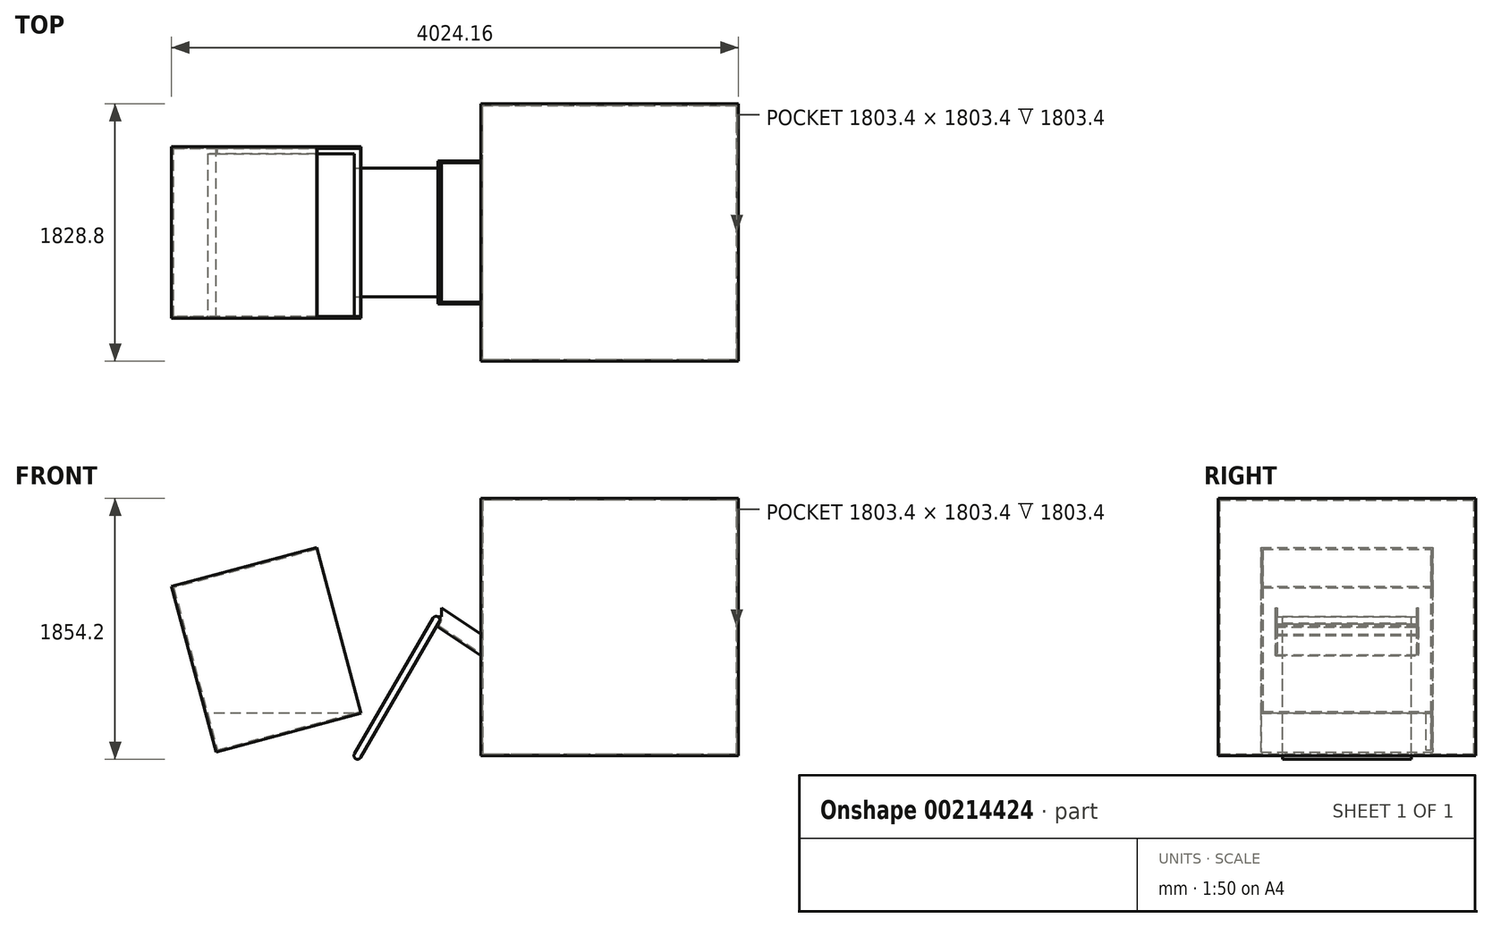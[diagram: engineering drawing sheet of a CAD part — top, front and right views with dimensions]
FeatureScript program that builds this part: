
annotation { "Feature Type Name" : "Feature", "Feature Type Description" : "" }
export const myFeature = defineFeature(function(context is Context, id is Id, definition is map)
    precondition{}
    {
        {
            var Q0;
            Q0=qCreatedBy(makeId("Front.planeOp"),FACE);
            var sketch = newSketch(context, id + "F0", { "sketchPlane" : qUnion([Q0])});
            skLineSegment(sketch, "E0", {"start": v(-22, 12.7) * mm, "end": v(535.26, 977.9) * mm});
            skCircle(sketch, "E1", {"center": v(557.26, 965.2) * mm, "radius": 25.4 * mm});
            skCircle(sketch, "E2", {"center": v(0, 0) * mm, "radius": 25.4 * mm});
            skLineSegment(sketch, "E3", {"start": v(22, -12.7) * mm, "end": v(579.26, 952.5) * mm});
            skLineSegment(sketch, "E4", {"start": v(569.96, 914.4) * mm, "end": v(874.76, 711.2) * mm});
            skLineSegment(sketch, "E5", {"start": v(874.76, 711.2) * mm, "end": v(874.76, 0) * mm});
            skLineSegment(sketch, "E6", {"start": v(874.76, 0) * mm, "end": v(2703.56, 0) * mm});
            skLineSegment(sketch, "E7", {"start": v(2703.56, 0) * mm, "end": v(2703.56, 1828.8) * mm});
            skLineSegment(sketch, "E8", {"start": v(2703.56, 1828.8) * mm, "end": v(874.76, 1828.8) * mm});
            skLineSegment(sketch, "E9", {"start": v(874.76, 1828.8) * mm, "end": v(874.76, 863.6) * mm});
            skLineSegment(sketch, "E10", {"start": v(874.76, 863.6) * mm, "end": v(569.96, 1066.8) * mm});
            skLineSegment(sketch, "E11", {"start": v(569.96, 1066.8) * mm, "end": v(569.96, 914.4) * mm});
            skSolve(sketch);
        }
        {
            var Q0;
            {var subQ7=sQuery(id+"F0.wireOp",EDGE,"E4");Q0=makeQuery(id+"F0.imprint","IMPRINT",FACE,{"disambiguationData":[TD([[makeQuery(id+"F0.imprint","IMPRINT",EDGE,{"derivedFrom":subQ7}),1.0]])]});}
            extrude(context, id + "F1", {"entities" : qUnion([Q0]), "endBound" : BoundingType.SYMMETRIC, "depth" : 1828.8 * mm});
        }
        {
            var Q0;
            {var subQ7=sQuery(id+"F0.wireOp",EDGE,"E0");Q0=makeQuery(id+"F0.imprint","IMPRINT",FACE,{"disambiguationData":[TD([[makeQuery(id+"F0.imprint","IMPRINT",EDGE,{"derivedFrom":subQ7}),-1.0]])]});}
            var Q1;
            {var subQ0=sQuery(id+"F0.wireOp",EDGE,"E2");var subQ1=makeQuery(id+"F0.imprint","INTERSECT",VERTEX,{"derivedFrom":[sQuery(id+"F0.wireOp",EDGE,"E0"),subQ0]});Q1=makeQuery(id+"F0.imprint","IMPRINT",FACE,{"disambiguationData":[TD([[makeQuery(id+"F0.imprint","IMPRINT",EDGE,{"disambiguationData":[TD([[subQ1,-1.0]])],"derivedFrom":subQ0}),1.0]])]});}
            var Q2;
            {var subQ0=sQuery(id+"F0.wireOp",EDGE,"E1");var subQ1=makeQuery(id+"F0.imprint","INTERSECT",VERTEX,{"derivedFrom":[subQ0,sQuery(id+"F0.wireOp",EDGE,"E3")]});Q2=makeQuery(id+"F0.imprint","IMPRINT",FACE,{"disambiguationData":[TD([[makeQuery(id+"F0.imprint","IMPRINT",EDGE,{"disambiguationData":[TD([[subQ1,1.0]])],"derivedFrom":subQ0}),1.0]])]});}
            var Q3;
            {var subQ0=sQuery(id+"F0.wireOp",EDGE,"E1");var subQ1=makeQuery(id+"F0.imprint","INTERSECT",VERTEX,{"derivedFrom":[sQuery(id+"F0.wireOp",EDGE,"E0"),subQ0]});Q3=makeQuery(id+"F0.imprint","IMPRINT",FACE,{"disambiguationData":[TD([[makeQuery(id+"F0.imprint","IMPRINT",EDGE,{"disambiguationData":[TD([[subQ1,1.0]])],"derivedFrom":subQ0}),1.0]])]});}
            extrude(context, id + "F2", {"entities" : qUnion([Q0, Q1, Q2, Q3]), "endBound" : BoundingType.SYMMETRIC, "depth" : 914.4 * mm});
        }
        {
            var Q0;
            Q0=qCreatedBy(makeId("Front.planeOp"),FACE);
            var sketch = newSketch(context, id + "F3", { "sketchPlane" : qUnion([Q0])});
            skLineSegment(sketch, "E12", {"start": v(-1320.6, 1203.06) * mm, "end": v(-1005.05, 25.4) * mm});
            skLineSegment(sketch, "E13", {"start": v(-1005.05, 25.4) * mm, "end": v(25.4, 301.5) * mm});
            skLineSegment(sketch, "E14", {"start": v(25.4, 301.5) * mm, "end": v(-290.15, 1479.16) * mm});
            skLineSegment(sketch, "E15", {"start": v(-290.15, 1479.16) * mm, "end": v(-1320.6, 1203.06) * mm});
            skSolve(sketch);
        }
        {
            var Q0;
            Q0=makeQuery(id+"F3.imprint","IMPRINT",FACE,{"disambiguationData":[TD([[makeQuery(id+"F3.imprint","IMPRINT",EDGE,{"derivedFrom":sQuery(id+"F3.wireOp",EDGE,"E12")}),1.0]])]});
            extrude(context, id + "F4", {"entities" : qUnion([Q0]), "endBound" : BoundingType.SYMMETRIC, "depth" : 1219.2 * mm});
        }
        {
            var Q0;
            Q0=makeQuery(id+"F4.opExtrude","SWEPT_FACE",FACE,{"disambiguationData":[OSD([sQuery(id+"F3.wireOp",EDGE,"E14")])]});
            shell(context, id + "F5", {"entities" : qUnion([Q0]), "thickness" : 12.7 * mm});
        }
        {
            var Q0;
            Q0=makeQuery(id+"F4.opExtrude","CAP_FACE",FACE,{"disambiguationData":[OSD([sQuery(id+"F3.wireOp",EDGE,"E12"),sQuery(id+"F3.wireOp",EDGE,"E13"),sQuery(id+"F3.wireOp",EDGE,"E14"),sQuery(id+"F3.wireOp",EDGE,"E15")])],"isStart":false});
            var sketch = newSketch(context, id + "F6", { "sketchPlane" : qUnion([Q0])});
            skLineSegment(sketch, "E16", {"start": v(25.4, 301.5) * mm, "end": v(-1079.03, 301.5) * mm});
            skLineSegment(sketch, "E17", {"start": v(-1079.03, 301.5) * mm, "end": v(-1005.05, 25.4) * mm});
            skLineSegment(sketch, "E18", {"start": v(-1005.05, 25.4) * mm, "end": v(25.4, 301.5) * mm});
            skSolve(sketch);
        }
        {
            var Q0;
            Q0=makeQuery(id+"F6.imprint","IMPRINT",FACE,{"disambiguationData":[TD([[makeQuery(id+"F6.imprint","IMPRINT",EDGE,{"derivedFrom":sQuery(id+"F6.wireOp",EDGE,"E16")}),1.0]])]});
            extrude(context, id + "F7", {"entities" : qUnion([Q0]), "operationType" : NewBodyOperationType.ADD, "oppositeDirection" : true, "depth" : 1168.4 * mm});
        }
        {
            var Q0;
            Q0=makeQuery(id+"F1.opExtrude","SWEPT_FACE",FACE,{"disambiguationData":[OSD([sQuery(id+"F0.wireOp",EDGE,"E8")])]});
            var sketch = newSketch(context, id + "F8", { "sketchPlane" : qUnion([Q0])});
            skLineSegment(sketch, "E19.bottom", {"start": v(569.96, 914.4) * mm, "end": v(874.76, 914.4) * mm});
            skLineSegment(sketch, "E19.top", {"start": v(569.96, 508) * mm, "end": v(874.76, 508) * mm});
            skLineSegment(sketch, "E19.left", {"start": v(569.96, 914.4) * mm, "end": v(569.96, 508) * mm});
            skLineSegment(sketch, "E19.right", {"start": v(874.76, 914.4) * mm, "end": v(874.76, 508) * mm});
            skLineSegment(sketch, "E20.bottom", {"start": v(569.96, -508) * mm, "end": v(874.76, -508) * mm});
            skLineSegment(sketch, "E20.top", {"start": v(569.96, -914.4) * mm, "end": v(874.76, -914.4) * mm});
            skLineSegment(sketch, "E20.left", {"start": v(569.96, -508) * mm, "end": v(569.96, -914.4) * mm});
            skLineSegment(sketch, "E20.right", {"start": v(874.76, -508) * mm, "end": v(874.76, -914.4) * mm});
            skSolve(sketch);
        }
        {
            var Q0;
            Q0=makeQuery(id+"F8.imprint","IMPRINT",FACE,{"disambiguationData":[TD([[makeQuery(id+"F8.imprint","IMPRINT",EDGE,{"derivedFrom":sQuery(id+"F8.wireOp",EDGE,"E20.bottom")}),-1.0]])]});
            var Q1;
            Q1=makeQuery(id+"F8.imprint","IMPRINT",FACE,{"disambiguationData":[TD([[makeQuery(id+"F8.imprint","IMPRINT",EDGE,{"derivedFrom":sQuery(id+"F8.wireOp",EDGE,"E19.bottom")}),-1.0]])]});
            extrude(context, id + "F9", {"entities" : qUnion([Q0, Q1]), "operationType" : NewBodyOperationType.REMOVE, "endBound" : BoundingType.THROUGH_ALL, "oppositeDirection" : true, "depth" : 25.4 * mm});
        }
        {
            var Q0;
            Q0=makeQuery(id+"F1.opExtrude","SWEPT_FACE",FACE,{"disambiguationData":[OSD([sQuery(id+"F0.wireOp",EDGE,"E10")])]});
            shell(context, id + "F10", {"entities" : qUnion([Q0]), "thickness" : 12.7 * mm});
        }
        {
            var Q0;
            Q0 = qSketchRegion(id + "F8", true);
            extrude(context, id + "F11", {"entities" : qUnion([Q0]), "operationType" : NewBodyOperationType.REMOVE, "endBound" : BoundingType.SYMMETRIC, "oppositeDirection" : true, "depth" : 889 * mm});
        }
        {
            var Q0;
            {var subQ0=sQuery(id+"F0.wireOp",EDGE,"E11");Q0=makeQuery(id+"F1.opExtrude","SWEPT_FACE",FACE,{"disambiguationData":[OSD([subQ0]),TDD([makeQuery(id+"F0.imprint","IMPRINT",EDGE,{"disambiguationData":[TD([[makeQuery(id+"F0.imprint","INTERSECT",VERTEX,{"derivedFrom":[sQuery(id+"F0.wireOp",EDGE,"E10"),subQ0]}),-1.0]])],"derivedFrom":subQ0})])]});}
            var sketch = newSketch(context, id + "F12", { "sketchPlane" : qUnion([Q0])});
            skSolve(sketch);
        }
        {
            var Q0;
            {var subQ0=sQuery(id+"F0.wireOp",EDGE,"E11");var subQ1=sQuery(id+"F0.wireOp",EDGE,"E10");Q0=makeQuery(id+"F12.imprint","IMPRINT",FACE,{"disambiguationData":[TD([[makeQuery(id+"F12.imprint","IMPRINT",EDGE,{"derivedFrom":makeQuery(id+"F1.opExtrude","SWEPT_EDGE",EDGE,{"disambiguationData":[OSD([subQ1,subQ0])]})}),1.0]])]});}
            extrude(context, id + "F13", {"entities" : qUnion([Q0]), "operationType" : NewBodyOperationType.REMOVE, "oppositeDirection" : true, "depth" : 25.4 * mm});
        }
    });
